FCSTD DOCUMENT  (FreeCAD 1.0R39109 (Git))
Label: 040_table_bottom_assembly
License: All rights reserved
LicenseURL: http://en.wikipedia.org/wiki/All_rights_reserved
objects: App::FeaturePython×22, App::Link×8, Assembly::JointGroup×1, Assembly::AssemblyObject×1
EXTERNAL_REF file=042_table_bottom_leg_back_left.FCStd obj=Body
EXTERNAL_REF file=043_table_bottom_leg_front_right.FCStd obj=Body
EXTERNAL_REF file=044_table_bottom_leg_back_right.FCStd obj=Body
EXTERNAL_REF file=045_table_bottom_frame_small.FCStd obj=Body
EXTERNAL_REF file=046_table_bottom_frame_large.FCStd obj=Body

FEATURE [App::Link] Body
  LinkedObject = -> <external 042_table_bottom_leg_back_left.FCStd>#Body
FEATURE [App::FeaturePython] GroundedJoint  # Assembly grounded joint (typed FeaturePython)
  ObjectToGround = -> Body
FEATURE [App::Link] Body001
  LinkPlacement = pos=(-3.39e-14,700,-2.35e-14) rot=(0,0,1;4.71239rad)
  LinkedObject = -> <external 042_table_bottom_leg_back_left.FCStd>#Body
  Placement = pos=(-3.39e-14,700,-2.35e-14) rot=(0,0,1;4.71239rad)
FEATURE [App::FeaturePython] Joint  label="Legt Left Back 1"  # Assembly joint (typed FeaturePython)
  Activated = true
  AngleMax = 0
  AngleMin = 0
  Detach1 = false
  Detach2 = false
  Distance = -600
  Distance2 = 0
  EnableAngleMax = false
  EnableAngleMin = false
  EnableLengthMax = false
  EnableLengthMin = false
  JointType = 5 (Distance)
  LengthMax = 0
  LengthMin = 0
  Placement1 = pos=(50,1.4676,-14.8856) rot=(-0.57735,-0.57735,0.57735;2.0944rad)
  Placement2 = pos=(1.4676,50,-14.8856) rot=(0,-0.707107,0.707107;3.14159rad)
  Reference1 = -> Assembly [Body001.Face6,Body001.Face6]
  Reference2 = -> Assembly [Body.Face5,Body.Face5]
FEATURE [App::FeaturePython] Joint001  label="Legt Left Back 2"  # Assembly joint (typed FeaturePython)
  Activated = true
  AngleMax = 0
  AngleMin = 0
  Detach1 = false
  Detach2 = false
  Distance = 0
  Distance2 = 0
  EnableAngleMax = false
  EnableAngleMin = false
  EnableLengthMax = false
  EnableLengthMin = false
  JointType = 5 (Distance)
  LengthMax = 0
  LengthMin = 0
  Placement1 = pos=(15,15,410) rot=(0,0,1;0rad)
  Placement2 = pos=(15,15,410) rot=(0,0,1;0rad)
  Reference1 = -> Assembly [Body001.Face9,Body001.Face9]
  Reference2 = -> Assembly [Body.Face9,Body.Face9]
FEATURE [App::FeaturePython] Joint002  label="Legt Left Back 3"  # Assembly joint (typed FeaturePython)
  Activated = true
  AngleMax = 0
  AngleMin = 0
  Detach1 = false
  Detach2 = false
  Distance = 0
  Distance2 = 0
  EnableAngleMax = false
  EnableAngleMin = false
  EnableLengthMax = false
  EnableLengthMin = false
  JointType = 5 (Distance)
  LengthMax = 0
  LengthMin = 0
  Placement1 = pos=(-50,9e-16,-55) rot=(0.57735,-0.57735,0.57735;4.18879rad)
  Placement2 = pos=(0,-50,-55) rot=(-1,0,0;1.5708rad)
  Reference1 = -> Assembly [Body.Face1,Body.Face1]
  Reference2 = -> Assembly [Body001.Face3,Body001.Vertex3]
FEATURE [App::Link] Body002
  LinkPlacement = pos=(1770,8.9e-15,1.22e-14) rot=(0,0,1;1.5708rad)
  LinkedObject = -> <external 043_table_bottom_leg_front_right.FCStd>#Body
  Placement = pos=(1770,8.9e-15,1.22e-14) rot=(0,0,1;1.5708rad)
FEATURE [App::FeaturePython] Joint003  label="Leg Right Front 1"  # Assembly joint (typed FeaturePython)
  Activated = true
  AngleMax = 0
  AngleMin = 0
  Detach1 = false
  Detach2 = false
  Distance = 0
  Distance2 = 0
  EnableAngleMax = false
  EnableAngleMin = false
  EnableLengthMax = false
  EnableLengthMin = false
  JointType = 5 (Distance)
  LengthMax = 0
  LengthMin = 0
  Placement1 = pos=(-2e-16,0,-410) rot=(0,0,1;0rad)
  Placement2 = pos=(0,0,-410) rot=(0,0,1;0rad)
  Reference1 = -> Assembly [Body.Face2,Body.Face2]
  Reference2 = -> Assembly [Body002.Face2,Body002.Face2]
FEATURE [App::FeaturePython] Joint004  label="Leg Right Front 2"  # Assembly joint (typed FeaturePython)
  Activated = true
  AngleMax = 0
  AngleMin = 0
  Detach1 = false
  Detach2 = false
  Distance = 0
  Distance2 = 0
  EnableAngleMax = false
  EnableAngleMin = false
  EnableLengthMax = false
  EnableLengthMin = false
  JointType = 5 (Distance)
  LengthMax = 0
  LengthMin = 0
  Placement1 = pos=(-9e-16,-50,-55) rot=(-1,0,0;1.5708rad)
  Placement2 = pos=(-50,0,-55) rot=(-0.57735,0.57735,-0.57735;2.0944rad)
  Reference1 = -> Assembly [Body.Face3,Body.Face3]
  Reference2 = -> Assembly [Body002.Face1,Body002.Vertex4]
FEATURE [App::FeaturePython] Joint005  label="Leg Right Front 3"  # Assembly joint (typed FeaturePython)
  Activated = true
  AngleMax = 0
  AngleMin = 0
  Detach1 = false
  Detach2 = false
  Distance = -1670
  Distance2 = 0
  EnableAngleMax = false
  EnableAngleMin = false
  EnableLengthMax = false
  EnableLengthMin = false
  JointType = 5 (Distance)
  LengthMax = 0
  LengthMin = 0
  Placement1 = pos=(50,1.4676,-14.8856) rot=(-0.57735,-0.57735,0.57735;2.0944rad)
  Placement2 = pos=(1.4676,50,-14.8856) rot=(0,-0.707107,0.707107;3.14159rad)
  Reference1 = -> Assembly [Body.Face6,Body.Face6]
  Reference2 = -> Assembly [Body002.Face5,Body002.Face5]
FEATURE [App::Link] Body003
  LinkPlacement = pos=(1770,700,1.4038e-12) rot=(0,0,1;3.14159rad)
  LinkedObject = -> <external 044_table_bottom_leg_back_right.FCStd>#Body
  Placement = pos=(1770,700,1.4038e-12) rot=(0,0,1;3.14159rad)
FEATURE [App::FeaturePython] Joint006  label="Leg Right Back 1"  # Assembly joint (typed FeaturePython)
  Activated = true
  AngleMax = 0
  AngleMin = 0
  Detach1 = false
  Detach2 = false
  Distance = 0
  Distance2 = 0
  EnableAngleMax = false
  EnableAngleMin = false
  EnableLengthMax = false
  EnableLengthMin = false
  JointType = 5 (Distance)
  LengthMax = 0
  LengthMin = 0
  Placement1 = pos=(0,0,-410) rot=(0,0,1;0rad)
  Placement2 = pos=(-2e-16,0,-410) rot=(0,0,1;0rad)
  Reference1 = -> Assembly [Body003.Face2,Body003.Face2]
  Reference2 = -> Assembly [Body.Face2,Body.Face2]
FEATURE [App::FeaturePython] Joint007  label="Leg Right Back 2"  # Assembly joint (typed FeaturePython)
  Activated = true
  AngleMax = 0
  AngleMin = 0
  Detach1 = false
  Detach2 = false
  Distance = 0
  Distance2 = 0
  EnableAngleMax = false
  EnableAngleMin = false
  EnableLengthMax = false
  EnableLengthMin = false
  JointType = 5 (Distance)
  LengthMax = 0
  LengthMin = 0
  Placement1 = pos=(0,-50,-55) rot=(-1,0,0;1.5708rad)
  Placement2 = pos=(-50,1e-15,-55) rot=(0.57735,-0.57735,0.57735;4.18879rad)
  Reference1 = -> Assembly [Body003.Face3,Body003.Face3]
  Reference2 = -> Assembly [Body001.Face1,Body001.Vertex1]
FEATURE [App::FeaturePython] Joint008  label="Leg Right Back 3"  # Assembly joint (typed FeaturePython)
  Activated = true
  AngleMax = 0
  AngleMin = 0
  Detach1 = false
  Detach2 = false
  Distance = -1670
  Distance2 = 0
  EnableAngleMax = false
  EnableAngleMin = false
  EnableLengthMax = false
  EnableLengthMin = false
  JointType = 5 (Distance)
  LengthMax = 0
  LengthMin = 0
  Placement1 = pos=(1.4676,50,-14.8856) rot=(0,-0.707107,0.707107;3.14159rad)
  Placement2 = pos=(50,1.4676,-14.8856) rot=(-0.57735,-0.57735,0.57735;2.0944rad)
  Reference1 = -> Assembly [Body001.Face5,Body001.Face5]
  Reference2 = -> Assembly [Body003.Face6,Body003.Face6]
FEATURE [App::Link] Body004
  LinkPlacement = pos=(1770,350,-260) rot=(0,-0.707107,0.707107;3.14159rad)
  LinkedObject = -> <external 045_table_bottom_frame_small.FCStd>#Body
  Placement = pos=(1770,350,-260) rot=(0,-0.707107,0.707107;3.14159rad)
FEATURE [App::Link] Body005
  LinkPlacement = pos=(2e-15,350,-260) rot=(0,-0.707107,0.707107;3.14159rad)
  LinkedObject = -> <external 045_table_bottom_frame_small.FCStd>#Body
  Placement = pos=(2e-15,350,-260) rot=(0,-0.707107,0.707107;3.14159rad)
FEATURE [App::FeaturePython] Joint009  label="Distance"  # Assembly joint (typed FeaturePython)
  Activated = true
  AngleMax = 0
  AngleMin = 0
  Detach1 = false
  Detach2 = false
  Distance = 0
  Distance2 = 0
  EnableAngleMax = false
  EnableAngleMin = false
  EnableLengthMax = false
  EnableLengthMin = false
  JointType = 5 (Distance)
  LengthMax = 0
  LengthMin = 0
  Placement1 = pos=(2.274e-13,-5.68e-14,300) rot=(0,0,1;0rad)
  Placement2 = pos=(50,1.4676,-14.8856) rot=(-0.57735,-0.57735,0.57735;2.0944rad)
  Reference1 = -> Assembly [Body004.Face6,Body004.Face6]
  Reference2 = -> Assembly [Body002.Face6,Body002.Face6]
FEATURE [App::FeaturePython] Joint010  label="Distance001"  # Assembly joint (typed FeaturePython)
  Activated = true
  AngleMax = 0
  AngleMin = 0
  Detach1 = false
  Detach2 = false
  Distance = 0
  Distance2 = 0
  EnableAngleMax = false
  EnableAngleMin = false
  EnableLengthMax = false
  EnableLengthMin = false
  JointType = 5 (Distance)
  LengthMax = 0
  LengthMin = 0
  Placement1 = pos=(4e-16,-50,-55) rot=(-1,0,0;1.5708rad)
  Placement2 = pos=(-50,0,0) rot=(-0.57735,0.57735,-0.57735;2.0944rad)
  Reference1 = -> Assembly [Body002.Face3,Body002.Face3]
  Reference2 = -> Assembly [Body004.Face1,Body004.Vertex2]
FEATURE [App::FeaturePython] Joint011  label="Distance002"  # Assembly joint (typed FeaturePython)
  Activated = true
  AngleMax = 0
  AngleMin = 0
  Detach1 = false
  Detach2 = false
  Distance = -100
  Distance2 = 0
  EnableAngleMax = false
  EnableAngleMin = false
  EnableLengthMax = false
  EnableLengthMin = false
  JointType = 5 (Distance)
  LengthMax = 0
  LengthMin = 0
  Placement1 = pos=(0,50,5.68e-14) rot=(0,0.707107,-0.707107;3.14159rad)
  Placement2 = pos=(0,0,-410) rot=(0,0,1;0rad)
  Reference1 = -> Assembly [Body004.Face4,Body004.Vertex8]
  Reference2 = -> Assembly [Body002.Face2,Body002.Face2]
FEATURE [App::FeaturePython] Joint012  label="Distance003"  # Assembly joint (typed FeaturePython)
  Activated = true
  AngleMax = 0
  AngleMin = 0
  Detach1 = false
  Detach2 = false
  Distance = 0
  Distance2 = 0
  EnableAngleMax = false
  EnableAngleMin = false
  EnableLengthMax = false
  EnableLengthMin = false
  JointType = 5 (Distance)
  LengthMax = 0
  LengthMin = 0
  Placement1 = pos=(5e-16,0,300) rot=(0,0,1;0rad)
  Placement2 = pos=(1.4676,50,-14.8856) rot=(0,-0.707107,0.707107;3.14159rad)
  Reference1 = -> Assembly [Body005.Face6,Body005.Vertex4]
  Reference2 = -> Assembly [Body.Face5,Body.Vertex1]
FEATURE [App::FeaturePython] Joint013  label="Distance004"  # Assembly joint (typed FeaturePython)
  Activated = true
  AngleMax = 0
  AngleMin = 0
  Detach1 = false
  Detach2 = false
  Distance = 0
  Distance2 = 0
  EnableAngleMax = false
  EnableAngleMin = false
  EnableLengthMax = false
  EnableLengthMin = false
  JointType = 5 (Distance)
  LengthMax = 0
  LengthMin = 0
  Placement1 = pos=(-50,5.68e-14,0) rot=(-0.57735,0.57735,-0.57735;2.0944rad)
  Placement2 = pos=(50,1.4676,-14.8856) rot=(-0.57735,-0.57735,0.57735;2.0944rad)
  Reference1 = -> Assembly [Body005.Face1,Body005.Vertex4]
  Reference2 = -> Assembly [Body.Face6,Body.Face6]
FEATURE [App::FeaturePython] Joint014  label="Distance005"  # Assembly joint (typed FeaturePython)
  Activated = true
  AngleMax = 0
  AngleMin = 0
  Detach1 = false
  Detach2 = false
  Distance = 0
  Distance2 = 0
  EnableAngleMax = false
  EnableAngleMin = false
  EnableLengthMax = false
  EnableLengthMin = false
  JointType = 5 (Distance)
  LengthMax = 0
  LengthMin = 0
  Placement1 = pos=(-2e-16,-50,0) rot=(1,0,0;4.71239rad)
  Placement2 = pos=(-2.274e-13,-50,0) rot=(1,0,0;4.71239rad)
  Reference1 = -> Assembly [Body005.Face2,Body005.Vertex4]
  Reference2 = -> Assembly [Body004.Face2,Body004.Vertex3]
FEATURE [App::Link] Body006
  LinkPlacement = pos=(885,-25,-260) rot=(0,1,0;1.5708rad)
  LinkedObject = -> <external 046_table_bottom_frame_large.FCStd>#Body
  Placement = pos=(885,-25,-260) rot=(0,1,0;1.5708rad)
FEATURE [App::Link] Body007
  LinkPlacement = pos=(885,725,-260) rot=(0.707107,0,-0.707107;3.14159rad)
  LinkedObject = -> <external 046_table_bottom_frame_large.FCStd>#Body
  Placement = pos=(885,725,-260) rot=(0.707107,0,-0.707107;3.14159rad)
FEATURE [App::FeaturePython] Joint015  label="Distance006"  # Assembly joint (typed FeaturePython)
  Activated = true
  AngleMax = 0
  AngleMin = 0
  Detach1 = false
  Detach2 = false
  Distance = 0
  Distance2 = 0
  EnableAngleMax = false
  EnableAngleMin = false
  EnableLengthMax = false
  EnableLengthMin = false
  JointType = 5 (Distance)
  LengthMax = 0
  LengthMin = 0
  Placement1 = pos=(0,0,835) rot=(0,0,1;0rad)
  Placement2 = pos=(1.4676,50,-14.8856) rot=(0,-0.707107,0.707107;3.14159rad)
  Reference1 = -> Assembly [Body006.Face6,Body006.Face6]
  Reference2 = -> Assembly [Body002.Face5,Body002.Vertex6]
FEATURE [App::FeaturePython] Joint016  label="Distance007"  # Assembly joint (typed FeaturePython)
  Activated = true
  AngleMax = 0
  AngleMin = 0
  Detach1 = false
  Detach2 = false
  Distance = 0
  Distance2 = 0
  EnableAngleMax = false
  EnableAngleMin = false
  EnableLengthMax = false
  EnableLengthMin = false
  JointType = 5 (Distance)
  LengthMax = 0
  LengthMin = 0
  Placement1 = pos=(0,-25,0) rot=(-1,0,0;1.5708rad)
  Placement2 = pos=(-50,0,-55) rot=(-0.57735,0.57735,-0.57735;2.0944rad)
  Reference1 = -> Assembly [Body006.Face2,Body006.Vertex6]
  Reference2 = -> Assembly [Body002.Face1,Body002.Face1]
FEATURE [App::FeaturePython] Joint017  label="Distance008"  # Assembly joint (typed FeaturePython)
  Activated = true
  AngleMax = 0
  AngleMin = 0
  Detach1 = false
  Detach2 = false
  Distance = -100
  Distance2 = 0
  EnableAngleMax = false
  EnableAngleMin = false
  EnableLengthMax = false
  EnableLengthMin = false
  JointType = 5 (Distance)
  LengthMax = 0
  LengthMin = 0
  Placement1 = pos=(50,0,0) rot=(-0.57735,-0.57735,0.57735;2.0944rad)
  Placement2 = pos=(-2e-16,0,-410) rot=(0,0,1;0rad)
  Reference1 = -> Assembly [Body006.Face3,Body006.Vertex7]
  Reference2 = -> Assembly [Body.Face2,Body.Face2]
FEATURE [App::FeaturePython] Joint018  label="Distance009"  # Assembly joint (typed FeaturePython)
  Activated = true
  AngleMax = 0
  AngleMin = 0
  Detach1 = false
  Detach2 = false
  Distance = 0
  Distance2 = 0
  EnableAngleMax = false
  EnableAngleMin = false
  EnableLengthMax = false
  EnableLengthMin = false
  JointType = 5 (Distance)
  LengthMax = 0
  LengthMin = 0
  Placement1 = pos=(5.68e-14,1.137e-13,835) rot=(0,0,1;0rad)
  Placement2 = pos=(1.4676,50,-14.8856) rot=(0,-0.707107,0.707107;3.14159rad)
  Reference1 = -> Assembly [Body007.Face6,Body007.Face6]
  Reference2 = -> Assembly [Body001.Face5,Body001.Face5]
FEATURE [App::FeaturePython] Joint019  label="Distance010"  # Assembly joint (typed FeaturePython)
  Activated = true
  AngleMax = 0
  AngleMin = 0
  Detach1 = false
  Detach2 = false
  Distance = 0
  Distance2 = 0
  EnableAngleMax = false
  EnableAngleMin = false
  EnableLengthMax = false
  EnableLengthMin = false
  JointType = 5 (Distance)
  LengthMax = 0
  LengthMin = 0
  Placement1 = pos=(5.68e-14,-25,1.137e-13) rot=(-1,0,0;1.5708rad)
  Placement2 = pos=(-50,1e-15,-55) rot=(0.57735,-0.57735,0.57735;4.18879rad)
  Reference1 = -> Assembly [Body007.Face2,Body007.Vertex6]
  Reference2 = -> Assembly [Body001.Face1,Body001.Face1]
FEATURE [App::FeaturePython] Joint020  label="Distance011"  # Assembly joint (typed FeaturePython)
  Activated = true
  AngleMax = 0
  AngleMin = 0
  Detach1 = false
  Detach2 = false
  Distance = 0
  Distance2 = 0
  EnableAngleMax = false
  EnableAngleMin = false
  EnableLengthMax = false
  EnableLengthMin = false
  JointType = 5 (Distance)
  LengthMax = 0
  LengthMin = 0
  Placement1 = pos=(50,0,0) rot=(-0.57735,-0.57735,0.57735;2.0944rad)
  Placement2 = pos=(50,0,0) rot=(-0.57735,-0.57735,0.57735;2.0944rad)
  Reference1 = -> Assembly [Body006.Face3,Body006.Vertex7]
  Reference2 = -> Assembly [Body007.Face3,Body007.Vertex6]
FEATURE [Assembly::JointGroup] Joints
  Group = -> [GroundedJoint,Joint,Joint001,Joint002,Joint003,Joint004,Joint005,Joint006,Joint007,Joint008,Joint009,Joint010,Joint011,Joint012,Joint013,Joint014,Joint015,Joint016,Joint017,Joint018,Joint019,Joint020]
FEATURE [Assembly::AssemblyObject] Assembly
  Group = -> [Joints,Body,GroundedJoint,Body001,Joint,Joint001,Joint002,Body002,Joint003,Joint004,Joint005,Body003,Joint006,Joint007,Joint008,Body004,Body005,Joint009,Joint010,Joint011,Joint012,Joint013,Joint014,Body006,Body007,Joint015,Joint016,Joint017,Joint018,Joint019,Joint020]
  Origin = -> Origin
  Type = Assembly

RESOLVED EXTERNAL PARTS (link-assembly join: the EXTERNAL_REF files above that resolve inside this repo's crawl, each included once):
---- part 042_table_bottom_leg_back_left.FCStd = doc fcstd_a61766cc9059 ----
FCSTD DOCUMENT  (FreeCAD 1.0R39109 (Git))
Label: 042_table_bottom_leg_back_left
License: All rights reserved
LicenseURL: http://en.wikipedia.org/wiki/All_rights_reserved
objects: Sketcher::SketchObject×2, Spreadsheet::Sheet×1, PartDesign::Pad×1, PartDesign::Pocket×1, PartDesign::Body×1
note: 11 computed .brp shape members not serialized (recipe doc carries the construction recipe); baked Part::Feature solids carry a one-line shape summary decoded from their .brp

FEATURE [Sketcher::SketchObject] Sketch
  ArcFitTolerance = 1e-06
  AttachmentSupport = -> [XY_Plane]
  FullyConstrained = true
  MakeInternals = false
  MapMode = 5
  expr: Constraints[11] = Spreadsheet.width
  expr: Constraints[12] = Spreadsheet.length
  sketch-geometry (5):
    g0: LineSegment StartX=-50 StartY=50 StartZ=0 EndX=-50 EndY=-50 EndZ=0
    g1: LineSegment StartX=-50 StartY=-50 StartZ=0 EndX=50 EndY=-50 EndZ=0
    g2: LineSegment StartX=50 StartY=-50 StartZ=0 EndX=50 EndY=50 EndZ=0
    g3: LineSegment StartX=50 StartY=50 StartZ=0 EndX=-50 EndY=50 EndZ=0
    g4: LineSegment [constr] StartX=-50 StartY=50 StartZ=0 EndX=50 EndY=-50 EndZ=0
  constraints (13):
    c: Coincident(g0,g1)
    c: Coincident(g1,g2)
    c: Coincident(g2,g3)
    c: Coincident(g3,g0)
    c: Vertical(g0)
    c: Vertical(g2)
    c: Horizontal(g1)
    c: Horizontal(g3)
    c: Coincident(g4,g0)
    c: Coincident(g4,g1)
    c: Symmetric(g4,g4,g-1)
    c: Distance(g0,g0) = 100
    c: Distance(g3,g3) = 100
FEATURE [Spreadsheet::Sheet] Spreadsheet
  cells = A2='length; B2(length)=100; A3='width; B3(width)=100; A4='height; B4(height)=820
FEATURE [PartDesign::Pad] Pad
  Direction = (0,0,1)
  Length = 820
  Length2 = 10
  Midplane = true
  Profile = -> Sketch
  ReferenceAxis = -> Sketch [N_Axis]
  Suppressed = false
  Type = 0
  expr: Length = Spreadsheet.height
FEATURE [Sketcher::SketchObject] Sketch001
  ArcFitTolerance = 1e-06
  AttachmentOffset = pos=(0,0,410) rot=(0,0,1;0rad)
  AttachmentSupport = -> [XY_Plane]
  ExternalGeometry = -> [Pad]
  FullyConstrained = true
  MakeInternals = false
  MapMode = 5
  Placement = pos=(0,0,410) rot=(0,0,1;0rad)
  expr: .AttachmentOffset.Base.x = 0
  expr: .AttachmentOffset.Base.z = Spreadsheet.height / 2
  sketch-geometry (6):
    g0: LineSegment StartX=50 StartY=-50 StartZ=0 EndX=-50 EndY=-50 EndZ=0
    g1: LineSegment StartX=-50 StartY=-50 StartZ=0 EndX=-50 EndY=50 EndZ=0
    g2: LineSegment StartX=-50 StartY=50 StartZ=0 EndX=-20 EndY=50 EndZ=0
    g3: LineSegment StartX=-20 StartY=50 StartZ=0 EndX=-20 EndY=-20 EndZ=0
    g4: LineSegment StartX=-20 StartY=-20 StartZ=0 EndX=50 EndY=-20 EndZ=0
    g5: LineSegment StartX=50 StartY=-50 StartZ=0 EndX=50 EndY=-20 EndZ=0
  constraints (15):
    c: Coincident(g-5,g0)
    c: Coincident(g0,g-4)
    c: Coincident(g0,g1)
    c: Coincident(g1,g-6)
    c: Coincident(g1,g2)
    c: PointOnObject(g2,g-6)
    c: Coincident(g2,g3)
    c: Coincident(g3,g4)
    c: PointOnObject(g4,g-5)
    c: Horizontal(g4)
    c: Coincident(g0,g5)
    c: Coincident(g5,g4)
    c: Vertical(g3)
    c: Distance(g5,g5) = 30
    c: Equal(g5,g2)
FEATURE [PartDesign::Pocket] Pocket
  BaseFeature = -> Pad
  Direction = (0,0,-1)
  Length = 110
  Length2 = 5
  Profile = -> Sketch001
  ReferenceAxis = -> Sketch001 [N_Axis]
  Suppressed = false
  Type = 0
FEATURE [PartDesign::Body] Body
  AllowCompound = false
  Group = -> [Sketch,Pad,Sketch001,Pocket]
  Origin = -> Origin
  Tip = -> Pocket
---- part 043_table_bottom_leg_front_right.FCStd = doc fcstd_a38123629881 ----
FCSTD DOCUMENT  (FreeCAD 1.0R39109 (Git))
Label: 043_table_bottom_leg_front_right
License: All rights reserved
LicenseURL: http://en.wikipedia.org/wiki/All_rights_reserved
objects: Sketcher::SketchObject×2, Spreadsheet::Sheet×1, PartDesign::Pad×1, PartDesign::Pocket×1, PartDesign::Body×1
note: 11 computed .brp shape members not serialized (recipe doc carries the construction recipe); baked Part::Feature solids carry a one-line shape summary decoded from their .brp

FEATURE [Sketcher::SketchObject] Sketch
  ArcFitTolerance = 1e-06
  AttachmentSupport = -> [XY_Plane]
  FullyConstrained = true
  MakeInternals = false
  MapMode = 5
  expr: Constraints[11] = Spreadsheet.width
  expr: Constraints[12] = Spreadsheet.length
  sketch-geometry (5):
    g0: LineSegment StartX=-50 StartY=50 StartZ=0 EndX=-50 EndY=-50 EndZ=0
    g1: LineSegment StartX=-50 StartY=-50 StartZ=0 EndX=50 EndY=-50 EndZ=0
    g2: LineSegment StartX=50 StartY=-50 StartZ=0 EndX=50 EndY=50 EndZ=0
    g3: LineSegment StartX=50 StartY=50 StartZ=0 EndX=-50 EndY=50 EndZ=0
    g4: LineSegment [constr] StartX=-50 StartY=50 StartZ=0 EndX=50 EndY=-50 EndZ=0
  constraints (13):
    c: Coincident(g0,g1)
    c: Coincident(g1,g2)
    c: Coincident(g2,g3)
    c: Coincident(g3,g0)
    c: Vertical(g0)
    c: Vertical(g2)
    c: Horizontal(g1)
    c: Horizontal(g3)
    c: Coincident(g4,g0)
    c: Coincident(g4,g1)
    c: Symmetric(g4,g4,g-1)
    c: Distance(g0,g0) = 100
    c: Distance(g3,g3) = 100
FEATURE [Spreadsheet::Sheet] Spreadsheet
  cells = A2='length; B2(length)=100; A3='width; B3(width)=100; A4='height; B4(height)=820
FEATURE [PartDesign::Pad] Pad
  Direction = (0,0,1)
  Length = 820
  Length2 = 10
  Midplane = true
  Profile = -> Sketch
  ReferenceAxis = -> Sketch [N_Axis]
  Suppressed = false
  Type = 0
  expr: Length = Spreadsheet.height
FEATURE [Sketcher::SketchObject] Sketch001
  ArcFitTolerance = 1e-06
  AttachmentOffset = pos=(0,0,410) rot=(0,0,1;0rad)
  AttachmentSupport = -> [XY_Plane]
  ExternalGeometry = -> [Pad]
  FullyConstrained = true
  MakeInternals = false
  MapMode = 5
  Placement = pos=(0,0,410) rot=(0,0,1;0rad)
  expr: .AttachmentOffset.Base.x = 0
  expr: .AttachmentOffset.Base.z = Spreadsheet.height / 2
  sketch-geometry (6):
    g0: LineSegment StartX=50 StartY=-50 StartZ=0 EndX=-50 EndY=-50 EndZ=0
    g1: LineSegment StartX=-50 StartY=-50 StartZ=0 EndX=-50 EndY=50 EndZ=0
    g2: LineSegment StartX=-50 StartY=50 StartZ=0 EndX=-20 EndY=50 EndZ=0
    g3: LineSegment StartX=-20 StartY=50 StartZ=0 EndX=-20 EndY=-20 EndZ=0
    g4: LineSegment StartX=-20 StartY=-20 StartZ=0 EndX=50 EndY=-20 EndZ=0
    g5: LineSegment StartX=50 StartY=-50 StartZ=0 EndX=50 EndY=-20 EndZ=0
  constraints (15):
    c: Coincident(g-5,g0)
    c: Coincident(g0,g-4)
    c: Coincident(g0,g1)
    c: Coincident(g1,g-6)
    c: Coincident(g1,g2)
    c: PointOnObject(g2,g-6)
    c: Coincident(g2,g3)
    c: Coincident(g3,g4)
    c: PointOnObject(g4,g-5)
    c: Horizontal(g4)
    c: Coincident(g0,g5)
    c: Coincident(g5,g4)
    c: Vertical(g3)
    c: Distance(g5,g5) = 30
    c: Equal(g5,g2)
FEATURE [PartDesign::Pocket] Pocket
  BaseFeature = -> Pad
  Direction = (0,0,-1)
  Length = 110
  Length2 = 5
  Profile = -> Sketch001
  ReferenceAxis = -> Sketch001 [N_Axis]
  Suppressed = false
  Type = 0
FEATURE [PartDesign::Body] Body
  AllowCompound = false
  Group = -> [Sketch,Pad,Sketch001,Pocket]
  Origin = -> Origin
  Tip = -> Pocket
---- part 044_table_bottom_leg_back_right.FCStd = doc fcstd_b7bda2405223 ----
FCSTD DOCUMENT  (FreeCAD 1.0R39109 (Git))
Label: 043_table_bottom_leg_back_right
License: All rights reserved
LicenseURL: http://en.wikipedia.org/wiki/All_rights_reserved
objects: Sketcher::SketchObject×2, Spreadsheet::Sheet×1, PartDesign::Pad×1, PartDesign::Pocket×1, PartDesign::Body×1
note: 11 computed .brp shape members not serialized (recipe doc carries the construction recipe); baked Part::Feature solids carry a one-line shape summary decoded from their .brp

FEATURE [Sketcher::SketchObject] Sketch
  ArcFitTolerance = 1e-06
  AttachmentSupport = -> [XY_Plane]
  FullyConstrained = true
  MakeInternals = false
  MapMode = 5
  expr: Constraints[11] = Spreadsheet.width
  expr: Constraints[12] = Spreadsheet.length
  sketch-geometry (5):
    g0: LineSegment StartX=-50 StartY=50 StartZ=0 EndX=-50 EndY=-50 EndZ=0
    g1: LineSegment StartX=-50 StartY=-50 StartZ=0 EndX=50 EndY=-50 EndZ=0
    g2: LineSegment StartX=50 StartY=-50 StartZ=0 EndX=50 EndY=50 EndZ=0
    g3: LineSegment StartX=50 StartY=50 StartZ=0 EndX=-50 EndY=50 EndZ=0
    g4: LineSegment [constr] StartX=-50 StartY=50 StartZ=0 EndX=50 EndY=-50 EndZ=0
  constraints (13):
    c: Coincident(g0,g1)
    c: Coincident(g1,g2)
    c: Coincident(g2,g3)
    c: Coincident(g3,g0)
    c: Vertical(g0)
    c: Vertical(g2)
    c: Horizontal(g1)
    c: Horizontal(g3)
    c: Coincident(g4,g0)
    c: Coincident(g4,g1)
    c: Symmetric(g4,g4,g-1)
    c: Distance(g0,g0) = 100
    c: Distance(g3,g3) = 100
FEATURE [Spreadsheet::Sheet] Spreadsheet
  cells = A2='length; B2(length)=100; A3='width; B3(width)=100; A4='height; B4(height)=820
FEATURE [PartDesign::Pad] Pad
  Direction = (0,0,1)
  Length = 820
  Length2 = 10
  Midplane = true
  Profile = -> Sketch
  ReferenceAxis = -> Sketch [N_Axis]
  Suppressed = false
  Type = 0
  expr: Length = Spreadsheet.height
FEATURE [Sketcher::SketchObject] Sketch001
  ArcFitTolerance = 1e-06
  AttachmentOffset = pos=(0,0,410) rot=(0,0,1;0rad)
  AttachmentSupport = -> [XY_Plane]
  ExternalGeometry = -> [Pad]
  FullyConstrained = true
  MakeInternals = false
  MapMode = 5
  Placement = pos=(0,0,410) rot=(0,0,1;0rad)
  expr: .AttachmentOffset.Base.x = 0
  expr: .AttachmentOffset.Base.z = Spreadsheet.height / 2
  sketch-geometry (6):
    g0: LineSegment StartX=50 StartY=-50 StartZ=0 EndX=-50 EndY=-50 EndZ=0
    g1: LineSegment StartX=-50 StartY=-50 StartZ=0 EndX=-50 EndY=50 EndZ=0
    g2: LineSegment StartX=-50 StartY=50 StartZ=0 EndX=-20 EndY=50 EndZ=0
    g3: LineSegment StartX=-20 StartY=50 StartZ=0 EndX=-20 EndY=-20 EndZ=0
    g4: LineSegment StartX=-20 StartY=-20 StartZ=0 EndX=50 EndY=-20 EndZ=0
    g5: LineSegment StartX=50 StartY=-50 StartZ=0 EndX=50 EndY=-20 EndZ=0
  constraints (15):
    c: Coincident(g-5,g0)
    c: Coincident(g0,g-4)
    c: Coincident(g0,g1)
    c: Coincident(g1,g-6)
    c: Coincident(g1,g2)
    c: PointOnObject(g2,g-6)
    c: Coincident(g2,g3)
    c: Coincident(g3,g4)
    c: PointOnObject(g4,g-5)
    c: Horizontal(g4)
    c: Coincident(g0,g5)
    c: Coincident(g5,g4)
    c: Vertical(g3)
    c: Distance(g5,g5) = 30
    c: Equal(g5,g2)
FEATURE [PartDesign::Pocket] Pocket
  BaseFeature = -> Pad
  Direction = (0,0,-1)
  Length = 110
  Length2 = 5
  Profile = -> Sketch001
  ReferenceAxis = -> Sketch001 [N_Axis]
  Suppressed = false
  Type = 0
FEATURE [PartDesign::Body] Body
  AllowCompound = false
  Group = -> [Sketch,Pad,Sketch001,Pocket]
  Origin = -> Origin
  Tip = -> Pocket
---- part 045_table_bottom_frame_small.FCStd = doc fcstd_7d39cf70d16d ----
FCSTD DOCUMENT  (FreeCAD 1.0R39109 (Git))
Label: 045_table_bottom_frame_small
License: All rights reserved
LicenseURL: http://en.wikipedia.org/wiki/All_rights_reserved
objects: Sketcher::SketchObject×1, Spreadsheet::Sheet×1, PartDesign::Pad×1, PartDesign::Body×1
note: 6 computed .brp shape members not serialized (recipe doc carries the construction recipe); baked Part::Feature solids carry a one-line shape summary decoded from their .brp

FEATURE [Sketcher::SketchObject] Sketch
  ArcFitTolerance = 1e-06
  AttachmentSupport = -> [XY_Plane]
  FullyConstrained = true
  MakeInternals = false
  MapMode = 5
  expr: Constraints[11] = Spreadsheet.width
  expr: Constraints[12] = Spreadsheet.length
  sketch-geometry (5):
    g0: LineSegment StartX=-50 StartY=50 StartZ=0 EndX=-50 EndY=-50 EndZ=0
    g1: LineSegment StartX=-50 StartY=-50 StartZ=0 EndX=50 EndY=-50 EndZ=0
    g2: LineSegment StartX=50 StartY=-50 StartZ=0 EndX=50 EndY=50 EndZ=0
    g3: LineSegment StartX=50 StartY=50 StartZ=0 EndX=-50 EndY=50 EndZ=0
    g4: LineSegment [constr] StartX=-50 StartY=50 StartZ=0 EndX=50 EndY=-50 EndZ=0
  constraints (13):
    c: Coincident(g0,g1)
    c: Coincident(g1,g2)
    c: Coincident(g2,g3)
    c: Coincident(g3,g0)
    c: Vertical(g0)
    c: Vertical(g2)
    c: Horizontal(g1)
    c: Horizontal(g3)
    c: Coincident(g4,g0)
    c: Coincident(g4,g1)
    c: Symmetric(g4,g4,g-1)
    c: Distance(g0,g0) = 100
    c: Distance(g3,g3) = 100
FEATURE [Spreadsheet::Sheet] Spreadsheet
  cells = A2='length; B2(length)=100; A3='width; B3(width)=100; A4='height; B4(height)=600
FEATURE [PartDesign::Pad] Pad
  Direction = (0,0,1)
  Length = 600
  Length2 = 10
  Midplane = true
  Profile = -> Sketch
  ReferenceAxis = -> Sketch [N_Axis]
  Suppressed = false
  Type = 0
  expr: Length = Spreadsheet.height
FEATURE [PartDesign::Body] Body
  AllowCompound = false
  Group = -> [Sketch,Pad]
  Origin = -> Origin
  Tip = -> Pad
---- part 046_table_bottom_frame_large.FCStd = doc fcstd_a335ff6a4aca ----
FCSTD DOCUMENT  (FreeCAD 1.0R39109 (Git))
Label: 046_table_bottom_frame_large
License: All rights reserved
LicenseURL: http://en.wikipedia.org/wiki/All_rights_reserved
objects: Sketcher::SketchObject×1, Spreadsheet::Sheet×1, PartDesign::Pad×1, PartDesign::Body×1
note: 6 computed .brp shape members not serialized (recipe doc carries the construction recipe); baked Part::Feature solids carry a one-line shape summary decoded from their .brp

FEATURE [Sketcher::SketchObject] Sketch
  ArcFitTolerance = 1e-06
  AttachmentSupport = -> [XY_Plane]
  FullyConstrained = true
  MakeInternals = false
  MapMode = 5
  expr: Constraints[11] = Spreadsheet.width
  expr: Constraints[12] = Spreadsheet.length
  sketch-geometry (5):
    g0: LineSegment StartX=-50 StartY=25 StartZ=0 EndX=-50 EndY=-25 EndZ=0
    g1: LineSegment StartX=-50 StartY=-25 StartZ=0 EndX=50 EndY=-25 EndZ=0
    g2: LineSegment StartX=50 StartY=-25 StartZ=0 EndX=50 EndY=25 EndZ=0
    g3: LineSegment StartX=50 StartY=25 StartZ=0 EndX=-50 EndY=25 EndZ=0
    g4: LineSegment [constr] StartX=-50 StartY=25 StartZ=0 EndX=50 EndY=-25 EndZ=0
  constraints (13):
    c: Coincident(g0,g1)
    c: Coincident(g1,g2)
    c: Coincident(g2,g3)
    c: Coincident(g3,g0)
    c: Vertical(g0)
    c: Vertical(g2)
    c: Horizontal(g1)
    c: Horizontal(g3)
    c: Coincident(g4,g0)
    c: Coincident(g4,g1)
    c: Symmetric(g4,g4,g-1)
    c: Distance(g0,g0) = 50
    c: Distance(g3,g3) = 100
FEATURE [Spreadsheet::Sheet] Spreadsheet
  cells = A2='length; B2(length)=100; A3='width; B3(width)=50; A4='height; B4(height)=1670
FEATURE [PartDesign::Pad] Pad
  Direction = (0,0,1)
  Length = 1670
  Length2 = 10
  Midplane = true
  Profile = -> Sketch
  ReferenceAxis = -> Sketch [N_Axis]
  Suppressed = false
  Type = 0
  expr: Length = Spreadsheet.height
FEATURE [PartDesign::Body] Body
  AllowCompound = false
  Group = -> [Sketch,Pad]
  Origin = -> Origin
  Tip = -> Pad
